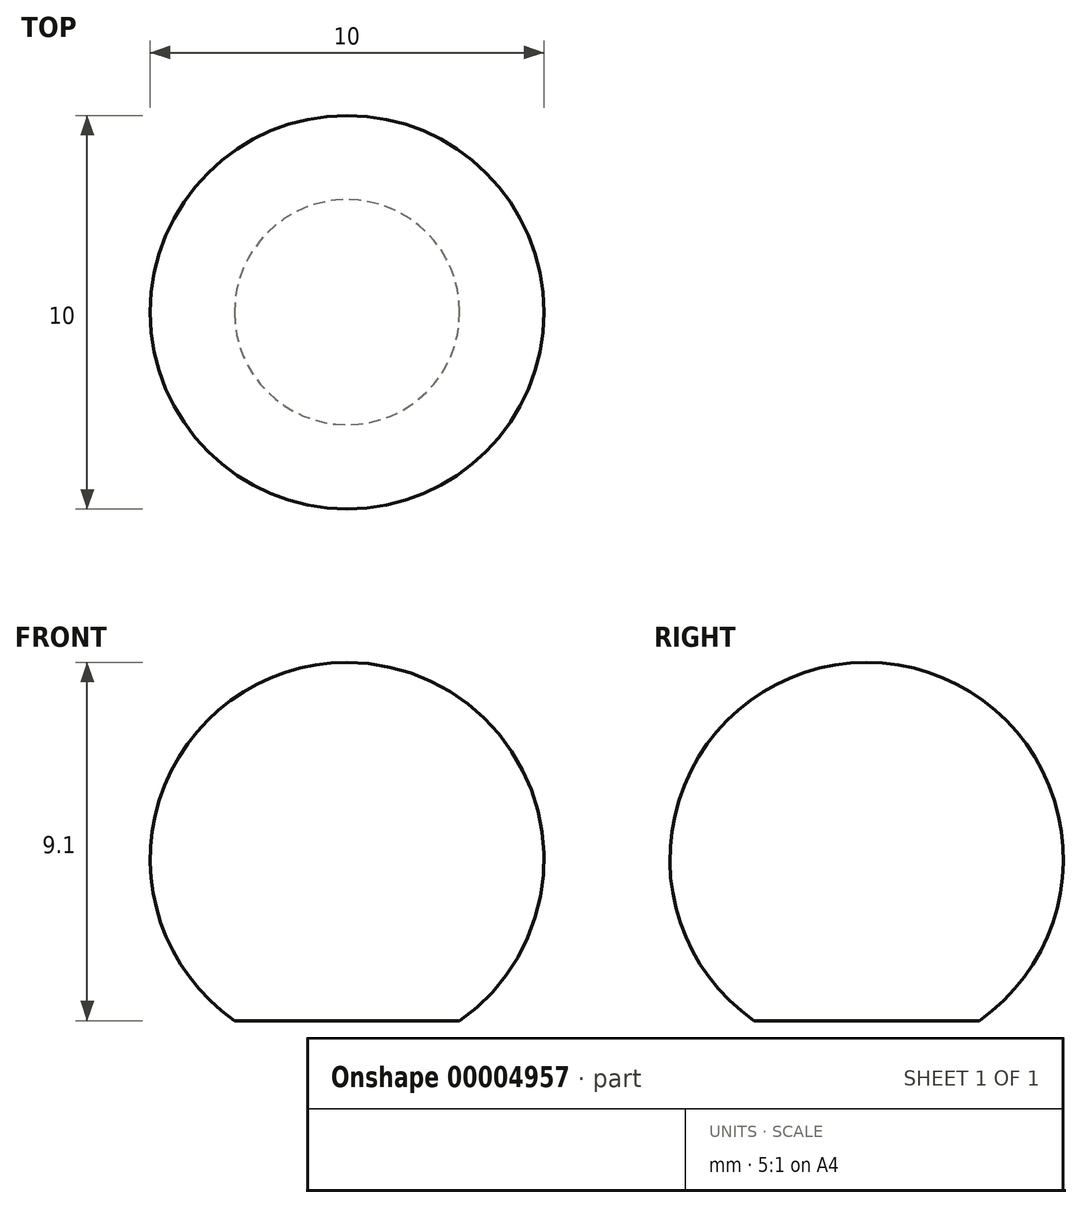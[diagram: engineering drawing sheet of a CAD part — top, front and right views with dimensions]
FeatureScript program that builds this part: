
annotation { "Feature Type Name" : "Feature", "Feature Type Description" : "" }
export const myFeature = defineFeature(function(context is Context, id is Id, definition is map)
    precondition{}
    {
        {
            var Q0;
            Q0=qCreatedBy(makeId("Front.planeOp"),FACE);
            var sketch = newSketch(context, id + "F0", { "sketchPlane" : qUnion([Q0])});
            skLineSegment(sketch, "E0", {"start": v(0, 0) * mm, "end": v(0, 9.1) * mm});
            skArc(sketch, "E1", {"start": v(2.86, 0) * mm, "mid": v(0, 9.1) * mm, "end": v(-2.86, 0) * mm});
            skLineSegment(sketch, "E2", {"start": v(-2.86, 0) * mm, "end": v(2.86, 0) * mm, "construction": true});
            skLineSegment(sketch, "E3", {"start": v(0, 0) * mm, "end": v(2.86, 0) * mm});
            skSolve(sketch);
        }
        {
            var Q0;
            Q0 = qSketchRegion(id + "F0", true);
            var Q1;
            Q1=sQuery(id+"F0.wireOp",EDGE,"E0");
            revolve(context, id + "F1", {"entities" : qUnion([Q0]), "axis" : qUnion([Q1]), "revolveType" : RevolveType.FULL});
        }
    });
